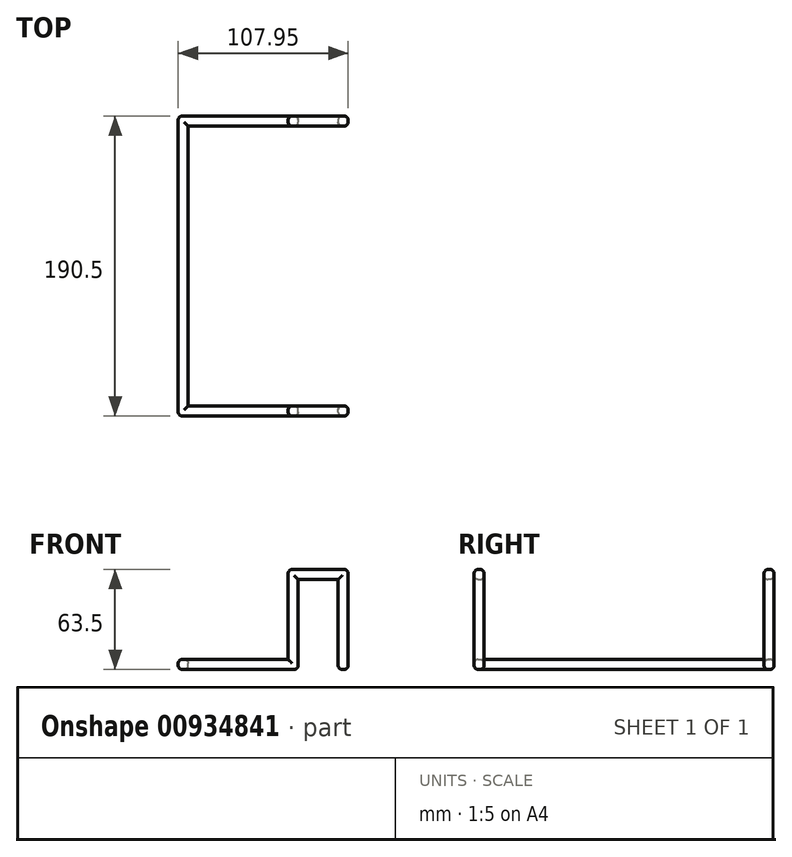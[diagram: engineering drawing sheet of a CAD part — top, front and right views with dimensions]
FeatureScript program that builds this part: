
annotation { "Feature Type Name" : "Feature", "Feature Type Description" : "" }
export const myFeature = defineFeature(function(context is Context, id is Id, definition is map)
    precondition{}
    {
        {
            var Q0;
            Q0=qCreatedBy(makeId("Front.planeOp"),FACE);
            var sketch = newSketch(context, id + "F0", { "sketchPlane" : qUnion([Q0])});
            skLineSegment(sketch, "E0.bottom", {"start": v(0, 0) * mm, "end": v(-6.35, 0) * mm});
            skLineSegment(sketch, "E0.top", {"start": v(0, 63.5) * mm, "end": v(-6.35, 63.5) * mm});
            skLineSegment(sketch, "E0.left", {"start": v(0, 0) * mm, "end": v(0, 63.5) * mm});
            skLineSegment(sketch, "E0.right", {"start": v(-6.35, 0) * mm, "end": v(-6.35, 63.5) * mm});
            skLineSegment(sketch, "E1.bottom", {"start": v(-6.35, 63.5) * mm, "end": v(31.75, 63.5) * mm});
            skLineSegment(sketch, "E1.top", {"start": v(-6.35, 57.15) * mm, "end": v(31.75, 57.15) * mm});
            skLineSegment(sketch, "E1.left", {"start": v(-6.35, 63.5) * mm, "end": v(-6.35, 57.15) * mm});
            skLineSegment(sketch, "E1.right", {"start": v(31.75, 63.5) * mm, "end": v(31.75, 57.15) * mm});
            skLineSegment(sketch, "E2.bottom", {"start": v(31.75, 63.5) * mm, "end": v(25.4, 63.5) * mm});
            skLineSegment(sketch, "E2.top", {"start": v(31.75, 0) * mm, "end": v(25.4, 0) * mm});
            skLineSegment(sketch, "E2.left", {"start": v(31.75, 63.5) * mm, "end": v(31.75, 0) * mm});
            skLineSegment(sketch, "E2.right", {"start": v(25.4, 63.5) * mm, "end": v(25.4, 0) * mm});
            skLineSegment(sketch, "E3.bottom", {"start": v(0, 0) * mm, "end": v(-76.2, 0) * mm});
            skLineSegment(sketch, "E3.top", {"start": v(0, 6.35) * mm, "end": v(-76.2, 6.35) * mm});
            skLineSegment(sketch, "E3.left", {"start": v(0, 0) * mm, "end": v(0, 6.35) * mm});
            skLineSegment(sketch, "E3.right", {"start": v(-76.2, 0) * mm, "end": v(-76.2, 6.35) * mm});
            skSolve(sketch);
        }
        {
            var Q0;
            Q0 = qSketchRegion(id + "F0", true);
            extrude(context, id + "F1", {"entities" : qUnion([Q0]), "depth" : 6.35 * mm, "offsetDistance" : 25.4 * mm});
        }
        {
            var Q0;
            Q0=qCreatedBy(makeId("Front.planeOp"),FACE);
            cPlane(context, id + "F2", {"entities" : qUnion([Q0]), "cplaneType" : CPlaneType.OFFSET, "offset" : 88.9 * mm, "oppositeDirection" : true, "width" : 152.4 * mm, "height" : 152.4 * mm});
        }
        {
            var Q0;
            Q0=makeQuery(id+"F1.opExtrude","SWEPT_BODY",BODY,{"disambiguationData":[OSD([sQuery(id+"F0.wireOp",EDGE,"E0.left"),sQuery(id+"F0.wireOp",EDGE,"E0.right"),sQuery(id+"F0.wireOp",EDGE,"E1.bottom"),sQuery(id+"F0.wireOp",EDGE,"E1.top"),sQuery(id+"F0.wireOp",EDGE,"E1.left"),sQuery(id+"F0.wireOp",EDGE,"E2.bottom"),sQuery(id+"F0.wireOp",EDGE,"E2.top"),sQuery(id+"F0.wireOp",EDGE,"E2.left"),sQuery(id+"F0.wireOp",EDGE,"E2.right"),sQuery(id+"F0.wireOp",EDGE,"E3.bottom"),sQuery(id+"F0.wireOp",EDGE,"E3.top"),sQuery(id+"F0.wireOp",EDGE,"E3.left"),sQuery(id+"F0.wireOp",EDGE,"E3.right")])]});
            var Q1;
            Q1=qCreatedBy(id+"F2.planeOp",FACE);
            mirror(context, id + "F3", {"entities" : qUnion([Q0]), "mirrorPlane" : qUnion([Q1])});
        }
        {
            var Q0;
            Q0=makeQuery(id+"F3.opPattern","COPY",FACE,{"derivedFrom":makeQuery(id+"F1.opExtrude","CAP_FACE",FACE,{"disambiguationData":[OSD([sQuery(id+"F0.wireOp",EDGE,"E0.left"),sQuery(id+"F0.wireOp",EDGE,"E0.right"),sQuery(id+"F0.wireOp",EDGE,"E1.bottom"),sQuery(id+"F0.wireOp",EDGE,"E1.top"),sQuery(id+"F0.wireOp",EDGE,"E1.left"),sQuery(id+"F0.wireOp",EDGE,"E2.bottom"),sQuery(id+"F0.wireOp",EDGE,"E2.top"),sQuery(id+"F0.wireOp",EDGE,"E2.left"),sQuery(id+"F0.wireOp",EDGE,"E2.right"),sQuery(id+"F0.wireOp",EDGE,"E3.bottom"),sQuery(id+"F0.wireOp",EDGE,"E3.top"),sQuery(id+"F0.wireOp",EDGE,"E3.left"),sQuery(id+"F0.wireOp",EDGE,"E3.right")])],"isStart":true}),"instanceName":"1"});
            var sketch = newSketch(context, id + "F4", { "sketchPlane" : qUnion([Q0])});
            skLineSegment(sketch, "E4.bottom", {"start": v(-76.2, 0) * mm, "end": v(-69.85, 0) * mm});
            skLineSegment(sketch, "E4.top", {"start": v(-76.2, 6.35) * mm, "end": v(-69.85, 6.35) * mm});
            skLineSegment(sketch, "E4.left", {"start": v(-76.2, 0) * mm, "end": v(-76.2, 6.35) * mm});
            skLineSegment(sketch, "E4.right", {"start": v(-69.85, 0) * mm, "end": v(-69.85, 6.35) * mm});
            skSolve(sketch);
        }
        {
            var Q0;
            Q0 = qSketchRegion(id + "F4", true);
            extrude(context, id + "F5", {"entities" : qUnion([Q0]), "operationType" : NewBodyOperationType.ADD, "depth" : 177.8 * mm, "offsetDistance" : 25.4 * mm});
        }
        {
            var Q0;
            Q0=makeQuery(id+"F1.opExtrude","CAP_EDGE",EDGE,{"disambiguationData":[OSD([sQuery(id+"F0.wireOp",EDGE,"E3.top")])],"isStart":false});
            var Q1;
            {var subQ0=makeQuery(id+"F1.opExtrude","SWEPT_EDGE",EDGE,{"disambiguationData":[OSD([sQuery(id+"F0.wireOp",EDGE,"E3.top"),sQuery(id+"F0.wireOp",EDGE,"E3.right")])]});Q1=makeQuery(id+"F5.boolean.opBoolean","MERGE",EDGE,{"derivedFrom":[subQ0,makeQuery(id+"F3.opPattern","COPY",EDGE,{"derivedFrom":subQ0,"instanceName":"1"}),makeQuery(id+"F5.opExtrude","SWEPT_EDGE",EDGE,{"disambiguationData":[OSD([sQuery(id+"F4.wireOp",EDGE,"E4.top"),sQuery(id+"F4.wireOp",EDGE,"E4.left")])]})]});}
            var Q2;
            Q2=makeQuery(id+"F5.opExtrude","SWEPT_EDGE",EDGE,{"disambiguationData":[OSD([sQuery(id+"F0.wireOp",EDGE,"E3.top"),sQuery(id+"F4.wireOp",EDGE,"E4.top"),sQuery(id+"F4.wireOp",EDGE,"E4.right")])]});
            var Q3;
            Q3=makeQuery(id+"F1.opExtrude","CAP_EDGE",EDGE,{"disambiguationData":[OSD([sQuery(id+"F0.wireOp",EDGE,"E3.top")])],"isStart":true});
            var Q4;
            Q4=makeQuery(id+"F5.opExtrude","SWEPT_EDGE",EDGE,{"disambiguationData":[OSD([sQuery(id+"F0.wireOp",EDGE,"E3.bottom"),sQuery(id+"F4.wireOp",EDGE,"E4.bottom"),sQuery(id+"F4.wireOp",EDGE,"E4.right")])]});
            var Q5;
            Q5=makeQuery(id+"F1.opExtrude","CAP_EDGE",EDGE,{"disambiguationData":[OSD([sQuery(id+"F0.wireOp",EDGE,"E0.right"),sQuery(id+"F0.wireOp",EDGE,"E1.left")])],"isStart":false});
            var Q6;
            Q6=makeQuery(id+"F1.opExtrude","CAP_EDGE",EDGE,{"disambiguationData":[OSD([sQuery(id+"F0.wireOp",EDGE,"E0.left"),sQuery(id+"F0.wireOp",EDGE,"E3.left")])],"isStart":false});
            var Q7;
            Q7=makeQuery(id+"F1.opExtrude","CAP_EDGE",EDGE,{"disambiguationData":[OSD([sQuery(id+"F0.wireOp",EDGE,"E1.bottom"),sQuery(id+"F0.wireOp",EDGE,"E2.bottom")])],"isStart":false});
            var Q8;
            Q8=makeQuery(id+"F1.opExtrude","CAP_EDGE",EDGE,{"disambiguationData":[OSD([sQuery(id+"F0.wireOp",EDGE,"E1.top")])],"isStart":false});
            var Q9;
            Q9=makeQuery(id+"F1.opExtrude","CAP_EDGE",EDGE,{"disambiguationData":[OSD([sQuery(id+"F0.wireOp",EDGE,"E1.bottom"),sQuery(id+"F0.wireOp",EDGE,"E2.bottom")])],"isStart":true});
            var Q10;
            Q10=makeQuery(id+"F1.opExtrude","CAP_EDGE",EDGE,{"disambiguationData":[OSD([sQuery(id+"F0.wireOp",EDGE,"E2.left")])],"isStart":false});
            var Q11;
            Q11=makeQuery(id+"F1.opExtrude","CAP_EDGE",EDGE,{"disambiguationData":[OSD([sQuery(id+"F0.wireOp",EDGE,"E2.right")])],"isStart":false});
            var Q12;
            Q12=makeQuery(id+"F1.opExtrude","CAP_EDGE",EDGE,{"disambiguationData":[OSD([sQuery(id+"F0.wireOp",EDGE,"E2.left")])],"isStart":true});
            var Q13;
            Q13=makeQuery(id+"F1.opExtrude","CAP_EDGE",EDGE,{"disambiguationData":[OSD([sQuery(id+"F0.wireOp",EDGE,"E3.bottom")])],"isStart":false});
            var Q14;
            Q14=makeQuery(id+"F1.opExtrude","CAP_EDGE",EDGE,{"disambiguationData":[OSD([sQuery(id+"F0.wireOp",EDGE,"E0.left"),sQuery(id+"F0.wireOp",EDGE,"E3.left")])],"isStart":true});
            var Q15;
            Q15=makeQuery(id+"F3.opPattern","COPY",EDGE,{"derivedFrom":makeQuery(id+"F1.opExtrude","CAP_EDGE",EDGE,{"disambiguationData":[OSD([sQuery(id+"F0.wireOp",EDGE,"E3.top")])],"isStart":true}),"instanceName":"1"});
            var Q16;
            Q16=makeQuery(id+"F3.opPattern","COPY",EDGE,{"derivedFrom":makeQuery(id+"F1.opExtrude","CAP_EDGE",EDGE,{"disambiguationData":[OSD([sQuery(id+"F0.wireOp",EDGE,"E3.top")])],"isStart":false}),"instanceName":"1"});
            var Q17;
            Q17=makeQuery(id+"F3.opPattern","COPY",EDGE,{"derivedFrom":makeQuery(id+"F1.opExtrude","CAP_EDGE",EDGE,{"disambiguationData":[OSD([sQuery(id+"F0.wireOp",EDGE,"E3.bottom")])],"isStart":true}),"instanceName":"1"});
            var Q18;
            Q18=makeQuery(id+"F3.opPattern","COPY",EDGE,{"derivedFrom":makeQuery(id+"F1.opExtrude","CAP_EDGE",EDGE,{"disambiguationData":[OSD([sQuery(id+"F0.wireOp",EDGE,"E0.left"),sQuery(id+"F0.wireOp",EDGE,"E3.left")])],"isStart":true}),"instanceName":"1"});
            var Q19;
            Q19=makeQuery(id+"F3.opPattern","COPY",EDGE,{"derivedFrom":makeQuery(id+"F1.opExtrude","CAP_EDGE",EDGE,{"disambiguationData":[OSD([sQuery(id+"F0.wireOp",EDGE,"E0.right"),sQuery(id+"F0.wireOp",EDGE,"E1.left")])],"isStart":true}),"instanceName":"1"});
            var Q20;
            Q20=makeQuery(id+"F3.opPattern","COPY",EDGE,{"derivedFrom":makeQuery(id+"F1.opExtrude","CAP_EDGE",EDGE,{"disambiguationData":[OSD([sQuery(id+"F0.wireOp",EDGE,"E0.left"),sQuery(id+"F0.wireOp",EDGE,"E3.left")])],"isStart":false}),"instanceName":"1"});
            var Q21;
            Q21=makeQuery(id+"F3.opPattern","COPY",EDGE,{"derivedFrom":makeQuery(id+"F1.opExtrude","CAP_EDGE",EDGE,{"disambiguationData":[OSD([sQuery(id+"F0.wireOp",EDGE,"E1.bottom"),sQuery(id+"F0.wireOp",EDGE,"E2.bottom")])],"isStart":true}),"instanceName":"1"});
            var Q22;
            Q22=makeQuery(id+"F3.opPattern","COPY",EDGE,{"derivedFrom":makeQuery(id+"F1.opExtrude","CAP_EDGE",EDGE,{"disambiguationData":[OSD([sQuery(id+"F0.wireOp",EDGE,"E1.top")])],"isStart":true}),"instanceName":"1"});
            var Q23;
            Q23=makeQuery(id+"F3.opPattern","COPY",EDGE,{"derivedFrom":makeQuery(id+"F1.opExtrude","CAP_EDGE",EDGE,{"disambiguationData":[OSD([sQuery(id+"F0.wireOp",EDGE,"E1.bottom"),sQuery(id+"F0.wireOp",EDGE,"E2.bottom")])],"isStart":false}),"instanceName":"1"});
            var Q24;
            Q24=makeQuery(id+"F3.opPattern","COPY",EDGE,{"derivedFrom":makeQuery(id+"F1.opExtrude","CAP_EDGE",EDGE,{"disambiguationData":[OSD([sQuery(id+"F0.wireOp",EDGE,"E2.left")])],"isStart":true}),"instanceName":"1"});
            var Q25;
            Q25=makeQuery(id+"F3.opPattern","COPY",EDGE,{"derivedFrom":makeQuery(id+"F1.opExtrude","CAP_EDGE",EDGE,{"disambiguationData":[OSD([sQuery(id+"F0.wireOp",EDGE,"E2.left")])],"isStart":false}),"instanceName":"1"});
            var Q26;
            Q26=makeQuery(id+"F3.opPattern","COPY",EDGE,{"derivedFrom":makeQuery(id+"F1.opExtrude","CAP_EDGE",EDGE,{"disambiguationData":[OSD([sQuery(id+"F0.wireOp",EDGE,"E2.right")])],"isStart":true}),"instanceName":"1"});
            fillet(context, id + "F6", {"entities" : qUnion([Q0, Q1, Q2, Q3, Q4, Q5, Q6, Q7, Q8, Q9, Q10, Q11, Q12, Q13, Q14, Q15, Q16, Q17, Q18, Q19, Q20, Q21, Q22, Q23, Q24, Q25, Q26]), "radius" : 2.54 * mm, "tangentPropagation" : true, "allowEdgeOverflow" : false});
        }
        {
            var Q0;
            Q0=makeQuery(id+"F1.opExtrude","CAP_EDGE",EDGE,{"disambiguationData":[OSD([sQuery(id+"F0.wireOp",EDGE,"E2.right")])],"isStart":true});
            var Q1;
            Q1=makeQuery(id+"F6.opFillet","BLEND_EDGE",EDGE,{"blendedFrom":[makeQuery(id+"F1.opExtrude","CAP_EDGE",EDGE,{"disambiguationData":[OSD([sQuery(id+"F0.wireOp",EDGE,"E2.left")])],"isStart":true}),makeQuery(id+"F1.opExtrude","SWEPT_FACE",FACE,{"disambiguationData":[OSD([sQuery(id+"F0.wireOp",EDGE,"E2.top")])]})],"blendedInto":[makeQuery(id+"F1.opExtrude","SWEPT_FACE",FACE,{"disambiguationData":[OSD([sQuery(id+"F0.wireOp",EDGE,"E2.top")])]})]});
            var Q2;
            Q2=makeQuery(id+"F6.opFillet","BLEND_EDGE",EDGE,{"blendedFrom":[makeQuery(id+"F3.opPattern","COPY",EDGE,{"derivedFrom":makeQuery(id+"F1.opExtrude","CAP_EDGE",EDGE,{"disambiguationData":[OSD([sQuery(id+"F0.wireOp",EDGE,"E2.left")])],"isStart":false}),"instanceName":"1"}),makeQuery(id+"F3.opPattern","COPY",FACE,{"derivedFrom":makeQuery(id+"F1.opExtrude","SWEPT_FACE",FACE,{"disambiguationData":[OSD([sQuery(id+"F0.wireOp",EDGE,"E2.top")])]}),"instanceName":"1"})],"blendedInto":[makeQuery(id+"F3.opPattern","COPY",FACE,{"derivedFrom":makeQuery(id+"F1.opExtrude","SWEPT_FACE",FACE,{"disambiguationData":[OSD([sQuery(id+"F0.wireOp",EDGE,"E2.top")])]}),"instanceName":"1"})]});
            var Q3;
            {var subQ0=sQuery(id+"F0.wireOp",EDGE,"E1.top");Q3=makeQuery(id+"F6.opFillet","BLEND_EDGE",EDGE,{"blendedFrom":[makeQuery(id+"F1.opExtrude","CAP_EDGE",EDGE,{"disambiguationData":[OSD([subQ0])],"isStart":false}),makeQuery(id+"F1.opExtrude","CAP_FACE",FACE,{"disambiguationData":[OSD([sQuery(id+"F0.wireOp",EDGE,"E0.left"),sQuery(id+"F0.wireOp",EDGE,"E0.right"),sQuery(id+"F0.wireOp",EDGE,"E1.bottom"),subQ0,sQuery(id+"F0.wireOp",EDGE,"E1.left"),sQuery(id+"F0.wireOp",EDGE,"E2.bottom"),sQuery(id+"F0.wireOp",EDGE,"E2.top"),sQuery(id+"F0.wireOp",EDGE,"E2.left"),sQuery(id+"F0.wireOp",EDGE,"E2.right"),sQuery(id+"F0.wireOp",EDGE,"E3.bottom"),sQuery(id+"F0.wireOp",EDGE,"E3.top"),sQuery(id+"F0.wireOp",EDGE,"E3.left"),sQuery(id+"F0.wireOp",EDGE,"E3.right")])],"isStart":false})],"blendedInto":[makeQuery(id+"F1.opExtrude","CAP_FACE",FACE,{"disambiguationData":[OSD([sQuery(id+"F0.wireOp",EDGE,"E0.left"),sQuery(id+"F0.wireOp",EDGE,"E0.right"),sQuery(id+"F0.wireOp",EDGE,"E1.bottom"),subQ0,sQuery(id+"F0.wireOp",EDGE,"E1.left"),sQuery(id+"F0.wireOp",EDGE,"E2.bottom"),sQuery(id+"F0.wireOp",EDGE,"E2.top"),sQuery(id+"F0.wireOp",EDGE,"E2.left"),sQuery(id+"F0.wireOp",EDGE,"E2.right"),sQuery(id+"F0.wireOp",EDGE,"E3.bottom"),sQuery(id+"F0.wireOp",EDGE,"E3.top"),sQuery(id+"F0.wireOp",EDGE,"E3.left"),sQuery(id+"F0.wireOp",EDGE,"E3.right")])],"isStart":false})]});}
            var Q4;
            Q4=makeQuery(id+"F1.opExtrude","CAP_EDGE",EDGE,{"disambiguationData":[OSD([sQuery(id+"F0.wireOp",EDGE,"E1.top")])],"isStart":true});
            var Q5;
            Q5=makeQuery(id+"F1.opExtrude","CAP_EDGE",EDGE,{"disambiguationData":[OSD([sQuery(id+"F0.wireOp",EDGE,"E3.bottom")])],"isStart":true});
            var Q6;
            {var subQ0=sQuery(id+"F0.wireOp",EDGE,"E3.bottom");Q6=makeQuery(id+"F6.opFillet","BLEND_EDGE",EDGE,{"blendedFrom":[makeQuery(id+"F1.opExtrude","CAP_EDGE",EDGE,{"disambiguationData":[OSD([subQ0])],"isStart":false}),makeQuery(id+"F1.opExtrude","CAP_FACE",FACE,{"disambiguationData":[OSD([sQuery(id+"F0.wireOp",EDGE,"E0.left"),sQuery(id+"F0.wireOp",EDGE,"E0.right"),sQuery(id+"F0.wireOp",EDGE,"E1.bottom"),sQuery(id+"F0.wireOp",EDGE,"E1.top"),sQuery(id+"F0.wireOp",EDGE,"E1.left"),sQuery(id+"F0.wireOp",EDGE,"E2.bottom"),sQuery(id+"F0.wireOp",EDGE,"E2.top"),sQuery(id+"F0.wireOp",EDGE,"E2.left"),sQuery(id+"F0.wireOp",EDGE,"E2.right"),subQ0,sQuery(id+"F0.wireOp",EDGE,"E3.top"),sQuery(id+"F0.wireOp",EDGE,"E3.left"),sQuery(id+"F0.wireOp",EDGE,"E3.right")])],"isStart":false})],"blendedInto":[makeQuery(id+"F1.opExtrude","CAP_FACE",FACE,{"disambiguationData":[OSD([sQuery(id+"F0.wireOp",EDGE,"E0.left"),sQuery(id+"F0.wireOp",EDGE,"E0.right"),sQuery(id+"F0.wireOp",EDGE,"E1.bottom"),sQuery(id+"F0.wireOp",EDGE,"E1.top"),sQuery(id+"F0.wireOp",EDGE,"E1.left"),sQuery(id+"F0.wireOp",EDGE,"E2.bottom"),sQuery(id+"F0.wireOp",EDGE,"E2.top"),sQuery(id+"F0.wireOp",EDGE,"E2.left"),sQuery(id+"F0.wireOp",EDGE,"E2.right"),subQ0,sQuery(id+"F0.wireOp",EDGE,"E3.top"),sQuery(id+"F0.wireOp",EDGE,"E3.left"),sQuery(id+"F0.wireOp",EDGE,"E3.right")])],"isStart":false})]});}
            var Q7;
            {var subQ0=makeQuery(id+"F1.opExtrude","SWEPT_EDGE",EDGE,{"disambiguationData":[OSD([sQuery(id+"F0.wireOp",EDGE,"E3.bottom"),sQuery(id+"F0.wireOp",EDGE,"E3.right")])]});Q7=makeQuery(id+"F5.boolean.opBoolean","MERGE",EDGE,{"derivedFrom":[subQ0,makeQuery(id+"F3.opPattern","COPY",EDGE,{"derivedFrom":subQ0,"instanceName":"1"}),makeQuery(id+"F5.opExtrude","SWEPT_EDGE",EDGE,{"disambiguationData":[OSD([sQuery(id+"F4.wireOp",EDGE,"E4.bottom"),sQuery(id+"F4.wireOp",EDGE,"E4.left")])]})]});}
            var Q8;
            {var subQ0=sQuery(id+"F4.wireOp",EDGE,"E4.bottom");var subQ1=sQuery(id+"F0.wireOp",EDGE,"E3.bottom");var subQ2=makeQuery(id+"F1.opExtrude","SWEPT_FACE",FACE,{"disambiguationData":[OSD([subQ1])]});Q8=makeQuery(id+"F6.opFillet","BLEND_EDGE",EDGE,{"blendedFrom":[makeQuery(id+"F5.opExtrude","SWEPT_EDGE",EDGE,{"disambiguationData":[OSD([subQ1,subQ0,sQuery(id+"F4.wireOp",EDGE,"E4.right")])]}),makeQuery(id+"F5.boolean.opBoolean","MERGE",FACE,{"derivedFrom":[subQ2,makeQuery(id+"F3.opPattern","COPY",FACE,{"derivedFrom":subQ2,"instanceName":"1"}),makeQuery(id+"F5.opExtrude","SWEPT_FACE",FACE,{"disambiguationData":[OSD([subQ0])]})]})],"blendedInto":[makeQuery(id+"F5.boolean.opBoolean","MERGE",FACE,{"derivedFrom":[subQ2,makeQuery(id+"F3.opPattern","COPY",FACE,{"derivedFrom":subQ2,"instanceName":"1"}),makeQuery(id+"F5.opExtrude","SWEPT_FACE",FACE,{"disambiguationData":[OSD([subQ0])]})]})]});}
            var Q9;
            Q9=makeQuery(id+"F3.opPattern","COPY",EDGE,{"derivedFrom":makeQuery(id+"F1.opExtrude","CAP_EDGE",EDGE,{"disambiguationData":[OSD([sQuery(id+"F0.wireOp",EDGE,"E3.bottom")])],"isStart":false}),"instanceName":"1"});
            var Q10;
            Q10=makeQuery(id+"F3.opPattern","COPY",EDGE,{"derivedFrom":makeQuery(id+"F1.opExtrude","CAP_EDGE",EDGE,{"disambiguationData":[OSD([sQuery(id+"F0.wireOp",EDGE,"E1.top")])],"isStart":false}),"instanceName":"1"});
            var Q11;
            Q11=makeQuery(id+"F3.opPattern","COPY",EDGE,{"derivedFrom":makeQuery(id+"F1.opExtrude","CAP_EDGE",EDGE,{"disambiguationData":[OSD([sQuery(id+"F0.wireOp",EDGE,"E0.right"),sQuery(id+"F0.wireOp",EDGE,"E1.left")])],"isStart":false}),"instanceName":"1"});
            var Q12;
            Q12=makeQuery(id+"F3.opPattern","COPY",EDGE,{"derivedFrom":makeQuery(id+"F1.opExtrude","CAP_EDGE",EDGE,{"disambiguationData":[OSD([sQuery(id+"F0.wireOp",EDGE,"E2.right")])],"isStart":false}),"instanceName":"1"});
            var Q13;
            {var subQ0=sQuery(id+"F0.wireOp",EDGE,"E3.top");var subQ1=makeQuery(id+"F1.opExtrude","SWEPT_EDGE",EDGE,{"disambiguationData":[OSD([subQ0,sQuery(id+"F0.wireOp",EDGE,"E3.right")])]});Q13=makeQuery(id+"F6.opFillet","BLEND_EDGE",EDGE,{"blendedFrom":[makeQuery(id+"F3.opPattern","COPY",EDGE,{"derivedFrom":makeQuery(id+"F1.opExtrude","CAP_EDGE",EDGE,{"disambiguationData":[OSD([subQ0])],"isStart":false}),"instanceName":"1"}),makeQuery(id+"F5.boolean.opBoolean","MERGE",EDGE,{"derivedFrom":[subQ1,makeQuery(id+"F3.opPattern","COPY",EDGE,{"derivedFrom":subQ1,"instanceName":"1"}),makeQuery(id+"F5.opExtrude","SWEPT_EDGE",EDGE,{"disambiguationData":[OSD([sQuery(id+"F4.wireOp",EDGE,"E4.top"),sQuery(id+"F4.wireOp",EDGE,"E4.left")])]})]})],"blendedInto":[]});}
            var Q14;
            Q14=makeQuery(id+"F6.opFillet","BLEND_EDGE",EDGE,{"blendedFrom":[makeQuery(id+"F3.opPattern","COPY",EDGE,{"derivedFrom":makeQuery(id+"F1.opExtrude","CAP_EDGE",EDGE,{"disambiguationData":[OSD([sQuery(id+"F0.wireOp",EDGE,"E1.bottom"),sQuery(id+"F0.wireOp",EDGE,"E2.bottom")])],"isStart":true}),"instanceName":"1"}),makeQuery(id+"F3.opPattern","COPY",EDGE,{"derivedFrom":makeQuery(id+"F1.opExtrude","CAP_EDGE",EDGE,{"disambiguationData":[OSD([sQuery(id+"F0.wireOp",EDGE,"E2.left")])],"isStart":true}),"instanceName":"1"})],"blendedInto":[]});
            var Q15;
            Q15=makeQuery(id+"F6.opFillet","BLEND_EDGE",EDGE,{"blendedFrom":[makeQuery(id+"F1.opExtrude","CAP_EDGE",EDGE,{"disambiguationData":[OSD([sQuery(id+"F0.wireOp",EDGE,"E1.bottom"),sQuery(id+"F0.wireOp",EDGE,"E2.bottom")])],"isStart":false}),makeQuery(id+"F1.opExtrude","CAP_EDGE",EDGE,{"disambiguationData":[OSD([sQuery(id+"F0.wireOp",EDGE,"E2.left")])],"isStart":false})],"blendedInto":[]});
            var Q16;
            Q16=makeQuery(id+"F6.opFillet","BLEND_EDGE",EDGE,{"blendedFrom":[makeQuery(id+"F1.opExtrude","CAP_EDGE",EDGE,{"disambiguationData":[OSD([sQuery(id+"F0.wireOp",EDGE,"E0.right"),sQuery(id+"F0.wireOp",EDGE,"E1.left")])],"isStart":false}),makeQuery(id+"F1.opExtrude","CAP_EDGE",EDGE,{"disambiguationData":[OSD([sQuery(id+"F0.wireOp",EDGE,"E1.bottom"),sQuery(id+"F0.wireOp",EDGE,"E2.bottom")])],"isStart":false})],"blendedInto":[]});
            fillet(context, id + "F7", {"entities" : qUnion([Q0, Q1, Q2, Q3, Q4, Q5, Q6, Q7, Q8, Q9, Q10, Q11, Q12, Q13, Q14, Q15, Q16]), "radius" : 2.54 * mm, "tangentPropagation" : true, "allowEdgeOverflow" : false});
        }
    });
